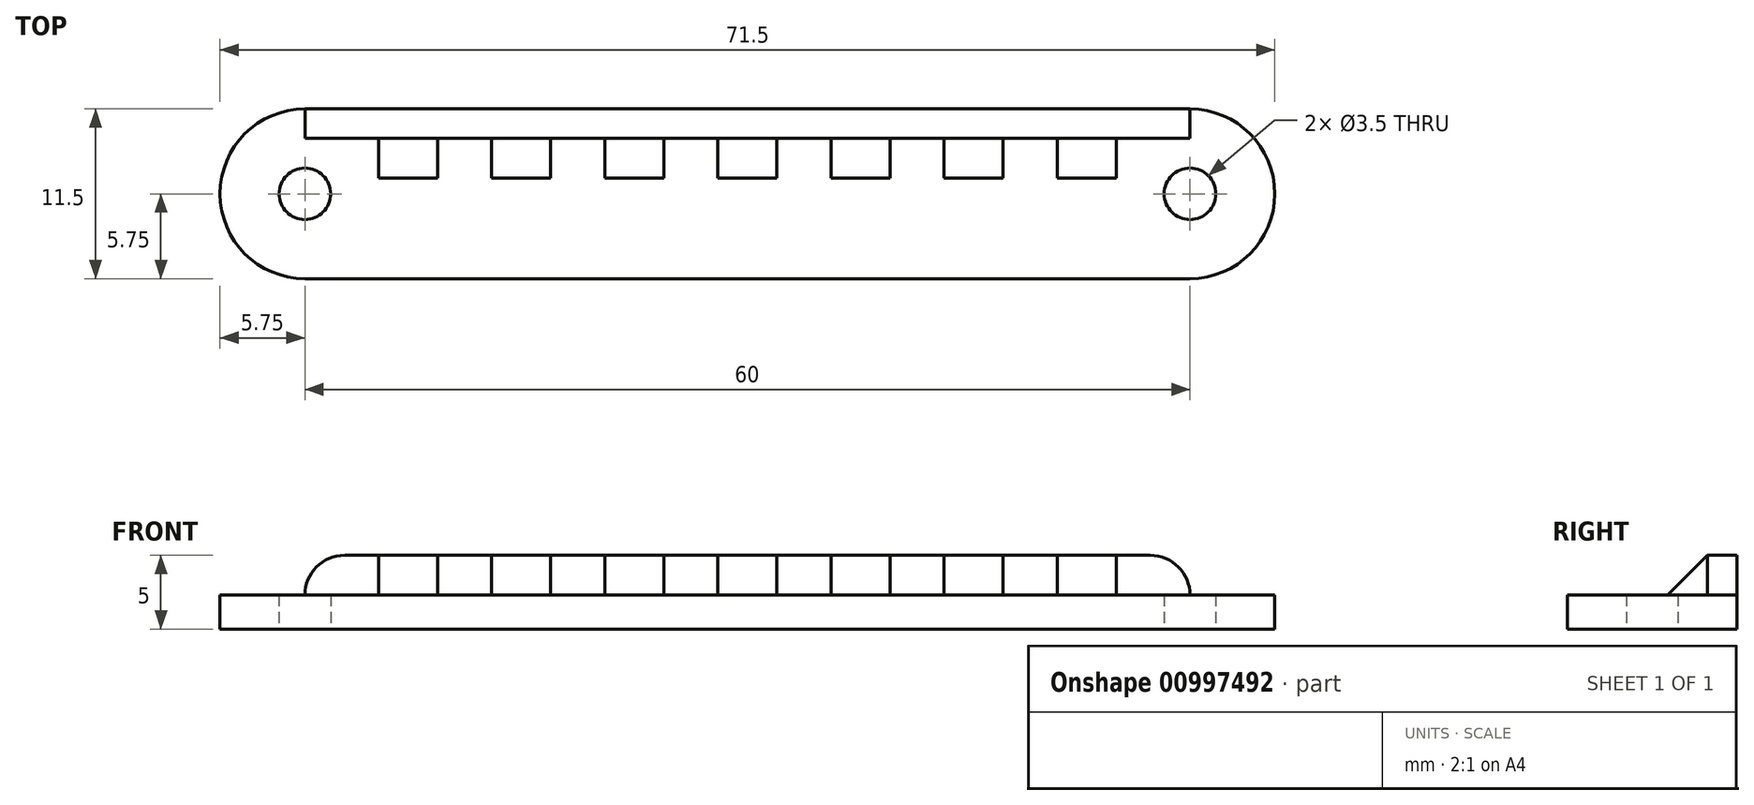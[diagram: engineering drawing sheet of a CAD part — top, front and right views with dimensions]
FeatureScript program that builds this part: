
annotation { "Feature Type Name" : "Feature", "Feature Type Description" : "" }
export const myFeature = defineFeature(function(context is Context, id is Id, definition is map)
    precondition{}
    {
        {
            var Q0;
            Q0=qCreatedBy(makeId("Top.planeOp"),FACE);
            var sketch = newSketch(context, id + "F0", { "sketchPlane" : qUnion([Q0])});
            skLineSegment(sketch, "E0", {"start": v(-30, 0) * mm, "end": v(30, 0) * mm, "construction": true});
            skPoint(sketch, "E1", {"position": v(0, 0) * mm});
            skCircle(sketch, "E2", {"center": v(-30, 0) * mm, "radius": 1.75 * mm});
            skCircle(sketch, "E3", {"center": v(30, 0) * mm, "radius": 1.75 * mm});
            skArc(sketch, "E4.0", {"start": v(-30, 5.75) * mm, "mid": v(-35.75, 0) * mm, "end": v(-30, -5.75) * mm});
            skLineSegment(sketch, "E5.0", {"start": v(-30, -5.75) * mm, "end": v(30, -5.75) * mm});
            skLineSegment(sketch, "E6.0", {"start": v(-30, 5.75) * mm, "end": v(30, 5.75) * mm});
            skArc(sketch, "E7.0", {"start": v(30, -5.75) * mm, "mid": v(35.75, 0) * mm, "end": v(30, 5.75) * mm});
            skLineSegment(sketch, "E8.0", {"start": v(-30, 3.75) * mm, "end": v(30, 3.75) * mm});
            skLineSegment(sketch, "E9", {"start": v(-30, 3.75) * mm, "end": v(-30, 5.75) * mm});
            skLineSegment(sketch, "E10", {"start": v(30, 3.75) * mm, "end": v(30, 5.75) * mm});
            skSolve(sketch);
        }
        {
            var Q0;
            Q0=makeQuery(id+"F0.imprint","IMPRINT",FACE,{"disambiguationData":[TD([[makeQuery(id+"F0.imprint","IMPRINT",EDGE,{"derivedFrom":sQuery(id+"F0.wireOp",EDGE,"E2")}),-1.0]])]});
            extrude(context, id + "F1", {"entities" : qUnion([Q0]), "depth" : 2.3 * mm, "offsetDistance" : 25 * mm});
        }
        {
            var Q0;
            Q0=makeQuery(id+"F0.imprint","IMPRINT",FACE,{"disambiguationData":[TD([[makeQuery(id+"F0.imprint","IMPRINT",EDGE,{"derivedFrom":sQuery(id+"F0.wireOp",EDGE,"E6.0")}),-1.0]])]});
            extrude(context, id + "F2", {"entities" : qUnion([Q0]), "operationType" : NewBodyOperationType.ADD, "depth" : 5 * mm, "offsetDistance" : 25 * mm});
        }
        {
            var Q0;
            Q0=makeQuery(id+"F1.opExtrude","CAP_FACE",FACE,{"disambiguationData":[OSD([sQuery(id+"F0.wireOp",EDGE,"E2"),sQuery(id+"F0.wireOp",EDGE,"E3"),sQuery(id+"F0.wireOp",EDGE,"E4.0"),sQuery(id+"F0.wireOp",EDGE,"E5.0"),sQuery(id+"F0.wireOp",EDGE,"E7.0"),sQuery(id+"F0.wireOp",EDGE,"E8.0"),sQuery(id+"F0.wireOp",EDGE,"E9"),sQuery(id+"F0.wireOp",EDGE,"E10")])],"isStart":false});
            var sketch = newSketch(context, id + "F3", { "sketchPlane" : qUnion([Q0])});
            skLineSegment(sketch, "E11", {"start": v(-28.25, 0) * mm, "end": v(-25, 0) * mm, "construction": true});
            skLineSegment(sketch, "E12", {"start": v(-25, 0) * mm, "end": v(-25, 3.75) * mm, "construction": true});
            skLineSegment(sketch, "E13", {"start": v(-25, 3.75) * mm, "end": v(-25, 1.05) * mm});
            skLineSegment(sketch, "E14", {"start": v(-25, 1.05) * mm, "end": v(-21, 1.05) * mm});
            skLineSegment(sketch, "E15", {"start": v(-21, 1.05) * mm, "end": v(-21, 3.75) * mm});
            skLineSegment(sketch, "E16", {"start": v(0, 0) * mm, "end": v(0, 3.75) * mm, "construction": true});
            skLineSegment(sketch, "E17.MirrorCS", {"start": v(28.25, 0) * mm, "end": v(25, 0) * mm, "construction": true});
            skLineSegment(sketch, "E18.MirrorCS", {"start": v(25, 0) * mm, "end": v(25, 3.75) * mm, "construction": true});
            skLineSegment(sketch, "E19.1.0.0", {"start": v(-17.33, 1.05) * mm, "end": v(-13.33, 1.05) * mm});
            skLineSegment(sketch, "E19.1.0.1", {"start": v(-13.33, 1.05) * mm, "end": v(-13.33, 3.75) * mm});
            skLineSegment(sketch, "E19.1.0.2", {"start": v(-17.33, 3.75) * mm, "end": v(-17.33, 1.05) * mm});
            skLineSegment(sketch, "E19.2.0.0", {"start": v(-9.67, 1.05) * mm, "end": v(-5.67, 1.05) * mm});
            skLineSegment(sketch, "E19.2.0.1", {"start": v(-5.67, 1.05) * mm, "end": v(-5.67, 3.75) * mm});
            skLineSegment(sketch, "E19.2.0.2", {"start": v(-9.67, 3.75) * mm, "end": v(-9.67, 1.05) * mm});
            skLineSegment(sketch, "E19.direction1", {"start": v(-25, 1.05) * mm, "end": v(-17.33, 1.05) * mm, "construction": true});
            skLineSegment(sketch, "E20.0.3.0", {"start": v(-2, 1.05) * mm, "end": v(2, 1.05) * mm});
            skLineSegment(sketch, "E20.3.3.0", {"start": v(2, 1.05) * mm, "end": v(2, 3.75) * mm});
            skLineSegment(sketch, "E20.6.3.0", {"start": v(-2, 3.75) * mm, "end": v(-2, 1.05) * mm});
            skLineSegment(sketch, "E20.0.4.0", {"start": v(5.67, 1.05) * mm, "end": v(9.67, 1.05) * mm});
            skLineSegment(sketch, "E20.3.4.0", {"start": v(9.67, 1.05) * mm, "end": v(9.67, 3.75) * mm});
            skLineSegment(sketch, "E20.6.4.0", {"start": v(5.67, 3.75) * mm, "end": v(5.67, 1.05) * mm});
            skLineSegment(sketch, "E20.0.5.0", {"start": v(13.33, 1.05) * mm, "end": v(17.33, 1.05) * mm});
            skLineSegment(sketch, "E20.3.5.0", {"start": v(17.33, 1.05) * mm, "end": v(17.33, 3.75) * mm});
            skLineSegment(sketch, "E20.6.5.0", {"start": v(13.33, 3.75) * mm, "end": v(13.33, 1.05) * mm});
            skLineSegment(sketch, "E20.0.6.0", {"start": v(21, 1.05) * mm, "end": v(25, 1.05) * mm});
            skLineSegment(sketch, "E20.3.6.0", {"start": v(25, 1.05) * mm, "end": v(25, 3.75) * mm});
            skLineSegment(sketch, "E20.6.6.0", {"start": v(21, 3.75) * mm, "end": v(21, 1.05) * mm});
            skSolve(sketch);
        }
        {
            var Q0;
            {var subQ0=sQuery(id+"F3.wireOp",EDGE,"E13");Q0=makeQuery(id+"F3.imprint","IMPRINT",FACE,{"disambiguationData":[TD([[makeQuery(id+"F3.imprint","IMPRINT",EDGE,{"derivedFrom":subQ0}),1.0]])]});}
            var Q1;
            Q1=makeQuery(id+"F3.imprint","IMPRINT",FACE,{"disambiguationData":[TD([[makeQuery(id+"F3.imprint","IMPRINT",EDGE,{"derivedFrom":sQuery(id+"F3.wireOp",EDGE,"E19.1.0.0")}),1.0]])]});
            var Q2;
            Q2=makeQuery(id+"F3.imprint","IMPRINT",FACE,{"disambiguationData":[TD([[makeQuery(id+"F3.imprint","IMPRINT",EDGE,{"derivedFrom":sQuery(id+"F3.wireOp",EDGE,"E19.2.0.0")}),1.0]])]});
            var Q3;
            Q3=makeQuery(id+"F3.imprint","IMPRINT",FACE,{"disambiguationData":[TD([[makeQuery(id+"F3.imprint","IMPRINT",EDGE,{"derivedFrom":sQuery(id+"F3.wireOp",EDGE,"E20.0.3.0")}),1.0]])]});
            var Q4;
            Q4=makeQuery(id+"F3.imprint","IMPRINT",FACE,{"disambiguationData":[TD([[makeQuery(id+"F3.imprint","IMPRINT",EDGE,{"derivedFrom":sQuery(id+"F3.wireOp",EDGE,"E20.0.4.0")}),1.0]])]});
            var Q5;
            Q5=makeQuery(id+"F3.imprint","IMPRINT",FACE,{"disambiguationData":[TD([[makeQuery(id+"F3.imprint","IMPRINT",EDGE,{"derivedFrom":sQuery(id+"F3.wireOp",EDGE,"E20.0.5.0")}),1.0]])]});
            var Q6;
            Q6=makeQuery(id+"F3.imprint","IMPRINT",FACE,{"disambiguationData":[TD([[makeQuery(id+"F3.imprint","IMPRINT",EDGE,{"derivedFrom":sQuery(id+"F3.wireOp",EDGE,"E20.0.6.0")}),1.0]])]});
            var Q7;
            Q7=makeQuery(id+"F2.opExtrude","CAP_FACE",FACE,{"disambiguationData":[OSD([sQuery(id+"F0.wireOp",EDGE,"E6.0"),sQuery(id+"F0.wireOp",EDGE,"E8.0"),sQuery(id+"F0.wireOp",EDGE,"E9"),sQuery(id+"F0.wireOp",EDGE,"E10")])],"isStart":false});
            extrude(context, id + "F4", {"entities" : qUnion([Q0, Q1, Q2, Q3, Q4, Q5, Q6]), "operationType" : NewBodyOperationType.ADD, "endBound" : BoundingType.UP_TO_SURFACE, "depth" : 25 * mm, "endBoundEntityFace" : qUnion([Q7]), "offsetDistance" : 25 * mm});
        }
        {
            var Q0;
            Q0=makeQuery(id+"F4.opExtrude","CAP_EDGE",EDGE,{"disambiguationData":[OSD([sQuery(id+"F3.wireOp",EDGE,"E14")])],"isStart":false});
            var Q1;
            Q1=makeQuery(id+"F4.opExtrude","CAP_EDGE",EDGE,{"disambiguationData":[OSD([sQuery(id+"F3.wireOp",EDGE,"E19.1.0.0")])],"isStart":false});
            var Q2;
            Q2=makeQuery(id+"F4.opExtrude","CAP_EDGE",EDGE,{"disambiguationData":[OSD([sQuery(id+"F3.wireOp",EDGE,"E19.2.0.0")])],"isStart":false});
            var Q3;
            Q3=makeQuery(id+"F4.opExtrude","CAP_EDGE",EDGE,{"disambiguationData":[OSD([sQuery(id+"F3.wireOp",EDGE,"E20.0.3.0")])],"isStart":false});
            var Q4;
            Q4=makeQuery(id+"F4.opExtrude","CAP_EDGE",EDGE,{"disambiguationData":[OSD([sQuery(id+"F3.wireOp",EDGE,"E20.0.4.0")])],"isStart":false});
            var Q5;
            Q5=makeQuery(id+"F4.opExtrude","CAP_EDGE",EDGE,{"disambiguationData":[OSD([sQuery(id+"F3.wireOp",EDGE,"E20.0.5.0")])],"isStart":false});
            var Q6;
            Q6=makeQuery(id+"F4.opExtrude","CAP_EDGE",EDGE,{"disambiguationData":[OSD([sQuery(id+"F3.wireOp",EDGE,"E20.0.6.0")])],"isStart":false});
            chamfer(context, id + "F5", {"entities" : qUnion([Q0, Q1, Q2, Q3, Q4, Q5, Q6]), "width" : 2.7 * mm, "tangentPropagation" : true});
        }
        {
            var Q0;
            Q0=makeQuery(id+"F2.opExtrude","CAP_EDGE",EDGE,{"disambiguationData":[OSD([sQuery(id+"F0.wireOp",EDGE,"E10")])],"isStart":false});
            var Q1;
            Q1=makeQuery(id+"F2.opExtrude","CAP_EDGE",EDGE,{"disambiguationData":[OSD([sQuery(id+"F0.wireOp",EDGE,"E9")])],"isStart":false});
            fillet(context, id + "F6", {"entities" : qUnion([Q0, Q1]), "radius" : 2.7 * mm, "tangentPropagation" : true, "allowEdgeOverflow" : false});
        }
    });
